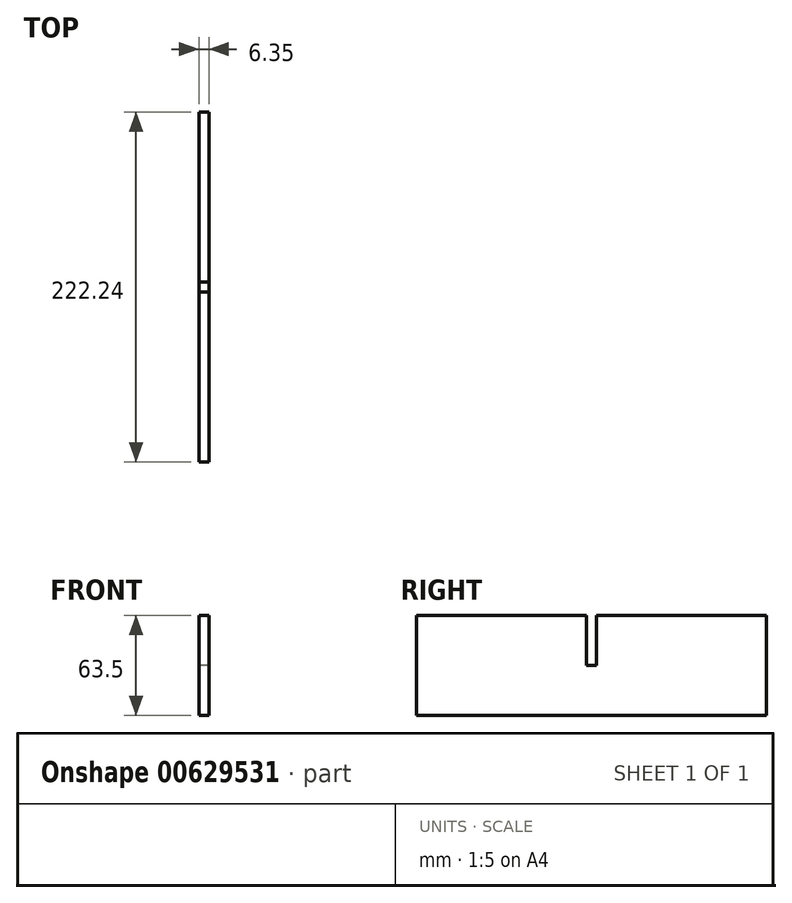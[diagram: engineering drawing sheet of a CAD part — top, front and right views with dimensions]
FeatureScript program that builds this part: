
annotation { "Feature Type Name" : "Feature", "Feature Type Description" : "" }
export const myFeature = defineFeature(function(context is Context, id is Id, definition is map)
    precondition{}
    {
        {
            var Q0;
            Q0=qCreatedBy(makeId("Right.planeOp"),FACE);
            var sketch = newSketch(context, id + "F0", { "sketchPlane" : qUnion([Q0])});
            skLineSegment(sketch, "E0", {"start": v(-111.13, 0) * mm, "end": v(111.13, 0) * mm});
            skLineSegment(sketch, "E1", {"start": v(111.13, 0) * mm, "end": v(111.12, 63.5) * mm});
            skLineSegment(sketch, "E2", {"start": v(111.12, 63.5) * mm, "end": v(3.17, 63.5) * mm});
            skLineSegment(sketch, "E3", {"start": v(3.17, 63.5) * mm, "end": v(3.17, 31.75) * mm});
            skLineSegment(sketch, "E4", {"start": v(3.17, 31.75) * mm, "end": v(-3.18, 31.75) * mm});
            skLineSegment(sketch, "E5", {"start": v(-3.18, 31.75) * mm, "end": v(-3.18, 63.5) * mm});
            skLineSegment(sketch, "E6", {"start": v(-3.18, 63.5) * mm, "end": v(-111.13, 63.5) * mm});
            skLineSegment(sketch, "E7", {"start": v(-111.13, 63.5) * mm, "end": v(-111.13, 0) * mm});
            skSolve(sketch);
        }
        {
            var Q0;
            Q0=makeQuery(id+"F0.imprint","IMPRINT",FACE,{"disambiguationData":[TD([[makeQuery(id+"F0.imprint","IMPRINT",EDGE,{"derivedFrom":sQuery(id+"F0.wireOp",EDGE,"E0")}),1.0]])]});
            extrude(context, id + "F1", {"entities" : qUnion([Q0]), "depth" : 6.35 * mm, "offsetDistance" : 25.4 * mm});
        }
    });
